# Revit family: FP_Revit_18_CI304PTX4_Cooktop_90001202B
name_source: partatom
category: Specialty Equipment
revit_build: Autodesk Revit 2018 (Build: 20170223_1515(x64)
units: mm (PartAtom-declared; Revit-internal decimal feet)

## family parameters
Always vertical = Yes
Cut with Voids When Loaded = Yes
OmniClass Number = 23.40.40.14.17.11
OmniClass Title = Cookers, Ovens, Stoves
Part Type = Normal
Room Calculation Point = No
Round Connector Dimension = Use Diameter
Shared = No
Work Plane-Based = No

## types (1)
- FP_Revit_18_CI304PTX4_Cooktop_90001202B
    Cavity - Depth = 490 mm  [stored 1.60761 ft]
    Cavity - Height = 85 mm  [stored 0.278871 ft]
    Cavity - Width = 730 mm  [stored 2.39501 ft]
    Chassis - Depth = 482 mm  [stored 1.58136 ft]
    Chassis - Height = 53 mm  [stored 0.173885 ft]
    Chassis - Width = 720 mm  [stored 2.3622 ft]
    Clearance - Below = 85 mm  [stored 0.278871 ft]
    Clearance - Overhead Combustible = 762 mm  [stored 2.5 ft]
    Clearance - Overhead Non-Combustible = 610 mm  [stored 2.00131 ft]
    Clearance - Overhead Rangehood = 650 mm  [stored 2.13255 ft]
    Clearance - Rear of cooktop to nearest Combustible Surface = 12 mm  [stored 0.0393701 ft]
    Clearance - Side of cooktop to nearest Combustible Surface = 14 mm  [stored 0.0459318 ft]
    Connector Note - Electrical = 208 or 240 V, 39 A or 45 A, 60 Hz,
    Description = 30" Induction Cooktop
    Manufacturer = Fisher & Paykel Appliances
    Material - Body = Fisher & Paykel - Grey
    Material - Glass = Fisher & Paykel - Glass, Black
    Material - Graphics = Fisher & Paykel - Graphics Grey
    Material - Trim = Fisher & Paykel - Stainless Steel
    Model = CI304PTX4
    Product - Depth = 533 mm
    Product - Height = 97 mm  [stored 0.318241 ft]
    Product - Width = 762 mm  [stored 2.5 ft]
    URL = www.fisherpaykel.com
    Visibility - Clearance Required = Yes

note: [stored X ft] marks values corroborated as IEEE doubles in the binary element streams (Revit-internal decimal feet)

## geometry (parser evidence)
native form markers: Sweep x11
no freeform markers — native parametric forms only
